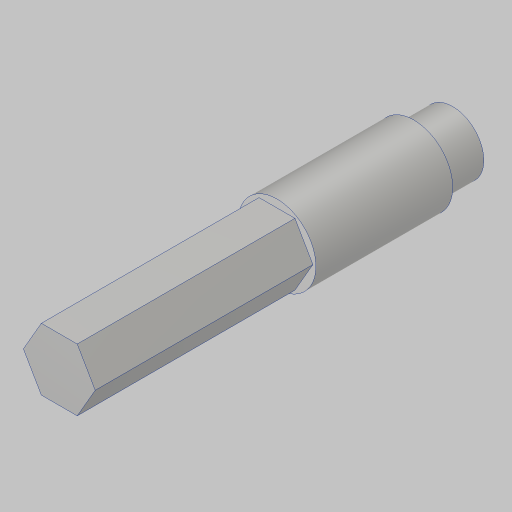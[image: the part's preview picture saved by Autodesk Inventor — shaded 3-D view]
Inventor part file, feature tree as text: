
AUTODESK INVENTOR PART (.ipt)
format: ipt  version: 2023.5 (Build 275446000, 446)  size: 146,944 bytes
history: native  units: in
note: dims shown in document units (in); Inventor stores cm internally (conversion verified against a paired STEP export)
features: extrude x5, sketch x5, projected_geometry x3
ambient origin geometry x8: Origin, YZ Plane, XZ Plane, XY Plane, X Axis, Y Axis, Z Axis, Center Point
bodies: Solid1 (feature_tree)
feature tree (13):
  extrude  "Extrusion1"  Depth=3.5625in TaperAngle=0.0deg
  extrude  "Extrusion2"  Depth=0.5in TaperAngle=0.0deg
  extrude  "Extrusion3"  Depth=0.25in TaperAngle=0.0deg
  extrude  "Extrusion6"  Depth=0.025in
  extrude  "Extrusion7"  Depth=0.5in
  sketch  "Sketch1"  dims[d0=0.625in d1=3.5625in d2=0.0in]
  sketch  "Sketch2"  dims[d3=0.5in d4=2.125in d5=0.0in]
  projected_geometry  "Projected Loop1"
  sketch  "Sketch3"  dims[d6=0.5in d7=0.25in d8=0.0in]
  projected_geometry  "Projected Loop2"
  sketch  "Sketch6"  dims[d15=0.375in d16=0.025in]
  sketch  "Sketch7"  dims[d17=1.0in d18=0.0in d19=0.5in d20=0.3125in d21=0.0in]
  projected_geometry  "Project Cut Edges3"
